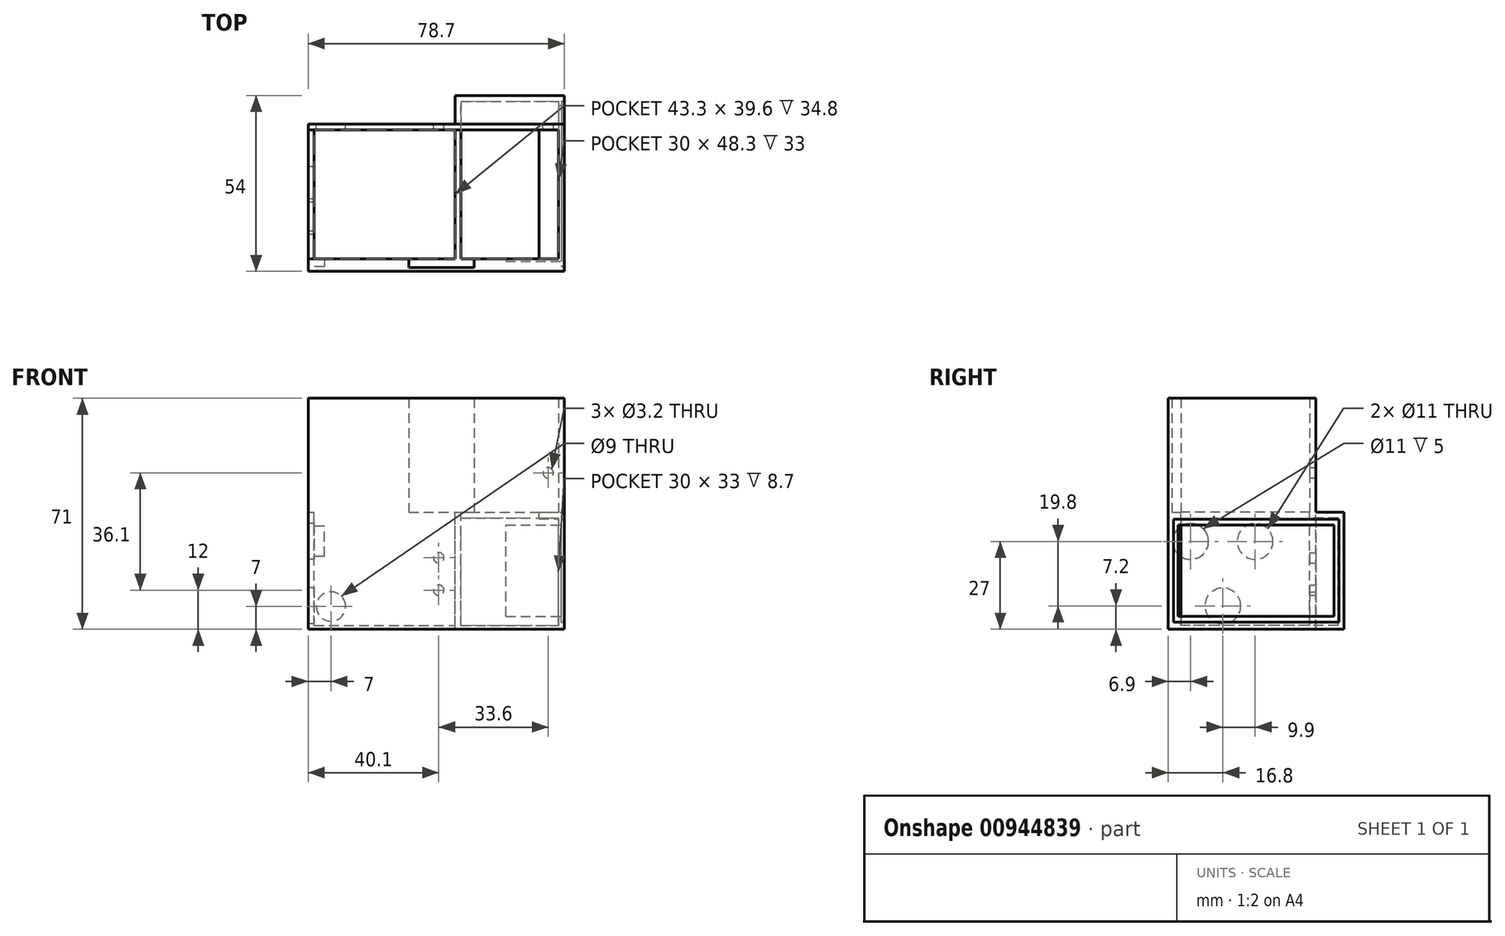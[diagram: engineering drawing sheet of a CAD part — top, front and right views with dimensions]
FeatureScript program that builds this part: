
annotation { "Feature Type Name" : "Feature", "Feature Type Description" : "" }
export const myFeature = defineFeature(function(context is Context, id is Id, definition is map)
    precondition{}
    {
        {
            var Q0;
            Q0=qCreatedBy(makeId("Top.planeOp"),FACE);
            var sketch = newSketch(context, id + "F0", { "sketchPlane" : qUnion([Q0])});
            skLineSegment(sketch, "E0.bottom", {"start": v(-38.45, 19.8) * mm, "end": v(38.45, 19.8) * mm});
            skLineSegment(sketch, "E0.top", {"start": v(-38.45, -19.8) * mm, "end": v(38.45, -19.8) * mm});
            skLineSegment(sketch, "E0.left", {"start": v(-38.45, 19.8) * mm, "end": v(-38.45, -19.8) * mm});
            skLineSegment(sketch, "E0.right", {"start": v(38.45, 19.8) * mm, "end": v(38.45, -19.8) * mm});
            skPoint(sketch, "E0.middle", {"position": v(0, 0) * mm});
            skLineSegment(sketch, "E1", {"start": v(-38.45, 19.8) * mm, "end": v(-38.45, 21.6) * mm});
            skLineSegment(sketch, "E2", {"start": v(-38.45, 21.6) * mm, "end": v(40.25, 21.6) * mm});
            skLineSegment(sketch, "E3", {"start": v(40.25, 21.6) * mm, "end": v(40.25, -23.7) * mm});
            skLineSegment(sketch, "E4", {"start": v(40.25, -23.7) * mm, "end": v(-38.45, -23.7) * mm});
            skLineSegment(sketch, "E5", {"start": v(-38.45, -23.7) * mm, "end": v(-38.45, -19.8) * mm});
            skLineSegment(sketch, "E6", {"start": v(-7.55, -19.8) * mm, "end": v(-7.55, -22.5) * mm});
            skLineSegment(sketch, "E7", {"start": v(-7.55, -22.5) * mm, "end": v(12.45, -22.5) * mm});
            skLineSegment(sketch, "E8", {"start": v(12.45, -22.5) * mm, "end": v(12.45, -19.8) * mm});
            skLineSegment(sketch, "E9", {"start": v(-36.65, 19.8) * mm, "end": v(-36.65, -19.8) * mm});
            skLineSegment(sketch, "E10", {"start": v(8.45, 19.8) * mm, "end": v(8.45, -19.8) * mm});
            skLineSegment(sketch, "E11", {"start": v(6.65, 19.8) * mm, "end": v(6.65, -19.8) * mm});
            skLineSegment(sketch, "E12", {"start": v(40.25, 21.6) * mm, "end": v(40.25, 30.3) * mm});
            skLineSegment(sketch, "E13", {"start": v(40.25, 30.3) * mm, "end": v(6.65, 30.3) * mm});
            skLineSegment(sketch, "E14", {"start": v(6.65, 30.3) * mm, "end": v(6.65, 21.6) * mm});
            skLineSegment(sketch, "E15", {"start": v(8.45, 21.6) * mm, "end": v(8.45, 28.5) * mm});
            skLineSegment(sketch, "E16", {"start": v(8.45, 28.5) * mm, "end": v(38.45, 28.5) * mm});
            skLineSegment(sketch, "E17", {"start": v(38.45, 28.5) * mm, "end": v(38.45, 21.6) * mm});
            skLineSegment(sketch, "E18", {"start": v(38.45, 21.6) * mm, "end": v(38.45, 19.8) * mm});
            skLineSegment(sketch, "E19", {"start": v(8.45, 21.6) * mm, "end": v(8.45, 19.8) * mm});
            skLineSegment(sketch, "E20", {"start": v(32.45, -19.8) * mm, "end": v(32.45, 19.8) * mm});
            skSolve(sketch);
        }
        {
            var Q0;
            {var subQ0=sQuery(id+"F0.wireOp",EDGE,"E1");Q0=makeQuery(id+"F0.imprint","IMPRINT",FACE,{"disambiguationData":[TD([[makeQuery(id+"F0.imprint","IMPRINT",EDGE,{"derivedFrom":subQ0}),-1.0]])]});}
            var Q1;
            {var subQ0=sQuery(id+"F0.wireOp",EDGE,"E18");Q1=makeQuery(id+"F0.imprint","IMPRINT",FACE,{"disambiguationData":[TD([[makeQuery(id+"F0.imprint","IMPRINT",EDGE,{"derivedFrom":subQ0}),-1.0]])]});}
            var Q2;
            {var subQ5=sQuery(id+"F0.wireOp",EDGE,"E0.right");Q2=makeQuery(id+"F0.imprint","IMPRINT",FACE,{"disambiguationData":[TD([[makeQuery(id+"F0.imprint","IMPRINT",EDGE,{"derivedFrom":subQ5}),1.0]])]});}
            extrude(context, id + "F1", {"entities" : qUnion([Q0, Q1, Q2]), "depth" : 35 * mm, "offsetDistance" : 25 * mm});
        }
        {
            var Q0;
            {var subQ0=sQuery(id+"F0.wireOp",EDGE,"E0.left");Q0=makeQuery(id+"F0.imprint","IMPRINT",FACE,{"disambiguationData":[TD([[makeQuery(id+"F0.imprint","IMPRINT",EDGE,{"derivedFrom":subQ0}),1.0]])]});}
            var Q1;
            {var subQ0=sQuery(id+"F0.wireOp",EDGE,"E1");Q1=makeQuery(id+"F0.imprint","IMPRINT",FACE,{"disambiguationData":[TD([[makeQuery(id+"F0.imprint","IMPRINT",EDGE,{"derivedFrom":subQ0}),-1.0]])]});}
            var Q2;
            {var subQ0=sQuery(id+"F0.wireOp",EDGE,"E12");Q2=makeQuery(id+"F0.imprint","IMPRINT",FACE,{"disambiguationData":[TD([[makeQuery(id+"F0.imprint","IMPRINT",EDGE,{"derivedFrom":subQ0}),1.0]])]});}
            var Q3;
            {var subQ5=sQuery(id+"F0.wireOp",EDGE,"E0.right");Q3=makeQuery(id+"F0.imprint","IMPRINT",FACE,{"disambiguationData":[TD([[makeQuery(id+"F0.imprint","IMPRINT",EDGE,{"derivedFrom":subQ5}),1.0]])]});}
            var Q4;
            {var subQ0=sQuery(id+"F0.wireOp",EDGE,"E6");Q4=makeQuery(id+"F0.imprint","IMPRINT",FACE,{"disambiguationData":[TD([[makeQuery(id+"F0.imprint","IMPRINT",EDGE,{"derivedFrom":subQ0}),1.0]])]});}
            var Q5;
            {var subQ0=sQuery(id+"F0.wireOp",EDGE,"E10");Q5=makeQuery(id+"F0.imprint","IMPRINT",FACE,{"disambiguationData":[TD([[makeQuery(id+"F0.imprint","IMPRINT",EDGE,{"derivedFrom":subQ0}),-1.0]])]});}
            extrude(context, id + "F2", {"entities" : qUnion([Q0, Q1, Q2, Q3, Q4, Q5]), "operationType" : NewBodyOperationType.ADD, "oppositeDirection" : true, "depth" : 36 * mm, "offsetDistance" : 25 * mm});
        }
        {
            var Q0;
            {var subQ0=sQuery(id+"F0.wireOp",EDGE,"E15");Q0=makeQuery(id+"F0.imprint","IMPRINT",FACE,{"disambiguationData":[TD([[makeQuery(id+"F0.imprint","IMPRINT",EDGE,{"derivedFrom":subQ0}),-1.0]])]});}
            var Q1;
            {var subQ0=sQuery(id+"F0.wireOp",EDGE,"E18");Q1=makeQuery(id+"F0.imprint","IMPRINT",FACE,{"disambiguationData":[TD([[makeQuery(id+"F0.imprint","IMPRINT",EDGE,{"derivedFrom":subQ0}),-1.0]])]});}
            extrude(context, id + "F3", {"entities" : qUnion([Q0, Q1]), "operationType" : NewBodyOperationType.ADD, "oppositeDirection" : true, "depth" : 1.8 * mm, "offsetDistance" : 25 * mm});
        }
        {
            var Q0;
            {var subQ0=sQuery(id+"F0.wireOp",EDGE,"E3");Q0=makeQuery(id+"F2.boolean.opBoolean","MERGE",FACE,{"derivedFrom":[makeQuery(id+"F1.opExtrude","SWEPT_FACE",FACE,{"disambiguationData":[OSD([subQ0])]}),makeQuery(id+"F2.opExtrude","SWEPT_FACE",FACE,{"disambiguationData":[OSD([subQ0,sQuery(id+"F0.wireOp",EDGE,"E12")])]})]});}
            var sketch = newSketch(context, id + "F4", { "sketchPlane" : qUnion([Q0])});
            skLineSegment(sketch, "E21.bottom", {"start": v(28.7, -33.8) * mm, "end": v(-22.1, -33.8) * mm});
            skLineSegment(sketch, "E21.top", {"start": v(28.7, -2.2) * mm, "end": v(-22.1, -2.2) * mm});
            skLineSegment(sketch, "E21.left", {"start": v(28.7, -33.8) * mm, "end": v(28.7, -2.2) * mm});
            skLineSegment(sketch, "E21.right", {"start": v(-22.1, -33.8) * mm, "end": v(-22.1, -2.2) * mm});
            skPoint(sketch, "E21.middle", {"position": v(3.3, -18) * mm});
            skPoint(sketch, "E21.middle.positionSnap0", {"position": v(30.3, -18) * mm});
            skPoint(sketch, "E21.middle.positionSnap1", {"position": v(3.3, -36) * mm});
            skPoint(sketch, "E21.centerSnap0", {"position": v(30.3, -18) * mm});
            skPoint(sketch, "E21.centerSnap1", {"position": v(3.3, -36) * mm});
            skLineSegment(sketch, "E22.bottom", {"start": v(27.2, -32) * mm, "end": v(-20.6, -32) * mm});
            skLineSegment(sketch, "E22.top", {"start": v(27.2, -4) * mm, "end": v(-20.6, -4) * mm});
            skLineSegment(sketch, "E22.left", {"start": v(27.2, -32) * mm, "end": v(27.2, -4) * mm});
            skLineSegment(sketch, "E22.right", {"start": v(-20.6, -32) * mm, "end": v(-20.6, -4) * mm});
            skSolve(sketch);
        }
        {
            var Q0;
            Q0=makeQuery(id+"F4.imprint","IMPRINT",FACE,{"disambiguationData":[TD([[makeQuery(id+"F4.imprint","IMPRINT",EDGE,{"derivedFrom":sQuery(id+"F4.wireOp",EDGE,"E22.bottom")}),-1.0]])]});
            extrude(context, id + "F5", {"entities" : qUnion([Q0]), "operationType" : NewBodyOperationType.REMOVE, "oppositeDirection" : true, "depth" : 18 * mm, "offsetDistance" : 25 * mm});
        }
        {
            var Q0;
            Q0=makeQuery(id+"F4.imprint","IMPRINT",FACE,{"disambiguationData":[TD([[makeQuery(id+"F4.imprint","IMPRINT",EDGE,{"derivedFrom":sQuery(id+"F4.wireOp",EDGE,"E21.bottom")}),-1.0]])]});
            extrude(context, id + "F6", {"entities" : qUnion([Q0]), "operationType" : NewBodyOperationType.REMOVE, "oppositeDirection" : true, "depth" : 1 * mm, "offsetDistance" : 25 * mm});
        }
        {
            var Q0;
            Q0=makeQuery(id+"F2.opExtrude","CAP_FACE",FACE,{"disambiguationData":[OSD([sQuery(id+"F0.wireOp",EDGE,"E0.bottom"),sQuery(id+"F0.wireOp",EDGE,"E0.top"),sQuery(id+"F0.wireOp",EDGE,"E0.left"),sQuery(id+"F0.wireOp",EDGE,"E0.right"),sQuery(id+"F0.wireOp",EDGE,"E1"),sQuery(id+"F0.wireOp",EDGE,"E2"),sQuery(id+"F0.wireOp",EDGE,"E3"),sQuery(id+"F0.wireOp",EDGE,"E4"),sQuery(id+"F0.wireOp",EDGE,"E5"),sQuery(id+"F0.wireOp",EDGE,"E9"),sQuery(id+"F0.wireOp",EDGE,"E10"),sQuery(id+"F0.wireOp",EDGE,"E11"),sQuery(id+"F0.wireOp",EDGE,"E12"),sQuery(id+"F0.wireOp",EDGE,"E13"),sQuery(id+"F0.wireOp",EDGE,"E14"),sQuery(id+"F0.wireOp",EDGE,"E15"),sQuery(id+"F0.wireOp",EDGE,"E16"),sQuery(id+"F0.wireOp",EDGE,"E17"),sQuery(id+"F0.wireOp",EDGE,"E18"),sQuery(id+"F0.wireOp",EDGE,"E19")])],"isStart":false});
            var sketch = newSketch(context, id + "F7", { "sketchPlane" : qUnion([Q0])});
            skSolve(sketch);
        }
        {
            var Q0;
            Q0=makeQuery(id+"F7.imprint","IMPRINT",FACE,{"disambiguationData":[TD([[makeQuery(id+"F7.imprint","IMPRINT",EDGE,{"derivedFrom":makeQuery(id+"F2.opExtrude","CAP_EDGE",EDGE,{"disambiguationData":[OSD([sQuery(id+"F0.wireOp",EDGE,"E0.bottom")])],"isStart":false})}),1.0]])]});
            var Q1;
            Q1=makeQuery(id+"F7.imprint","IMPRINT",FACE,{"disambiguationData":[TD([[makeQuery(id+"F7.imprint","IMPRINT",EDGE,{"derivedFrom":makeQuery(id+"F2.opExtrude","CAP_EDGE",EDGE,{"disambiguationData":[OSD([sQuery(id+"F0.wireOp",EDGE,"E16")])],"isStart":false})}),1.0]])]});
            extrude(context, id + "F8", {"entities" : qUnion([Q0, Q1]), "operationType" : NewBodyOperationType.ADD, "oppositeDirection" : true, "depth" : 1.2 * mm, "offsetDistance" : 25 * mm});
        }
        {
            var Q0;
            {var subQ0=sQuery(id+"F0.wireOp",EDGE,"E0.right");Q0=makeQuery(id+"F0.imprint","IMPRINT",FACE,{"disambiguationData":[TD([[makeQuery(id+"F0.imprint","IMPRINT",EDGE,{"derivedFrom":subQ0}),-1.0]])]});}
            extrude(context, id + "F9", {"entities" : qUnion([Q0]), "operationType" : NewBodyOperationType.ADD, "oppositeDirection" : true, "depth" : 2 * mm, "offsetDistance" : 25 * mm});
        }
        {
            var Q0;
            {var subQ0=sQuery(id+"F0.wireOp",EDGE,"E2");Q0=makeQuery(id+"F2.boolean.opBoolean","MERGE",FACE,{"derivedFrom":[makeQuery(id+"F1.opExtrude","SWEPT_FACE",FACE,{"disambiguationData":[OSD([subQ0])]}),makeQuery(id+"F2.opExtrude","SWEPT_FACE",FACE,{"disambiguationData":[OSD([subQ0])]})]});}
            var sketch = newSketch(context, id + "F10", { "sketchPlane" : qUnion([Q0])});
            skCircle(sketch, "E23", {"center": v(-35.25, 12.1) * mm, "radius": 1.6 * mm});
            skCircle(sketch, "E24", {"center": v(-1.65, -14) * mm, "radius": 1.6 * mm});
            skCircle(sketch, "E25", {"center": v(-1.65, -24) * mm, "radius": 1.6 * mm});
            skCircle(sketch, "E26", {"center": v(31.45, -29) * mm, "radius": 4.5 * mm});
            skSolve(sketch);
        }
        {
            var Q0;
            Q0=makeQuery(id+"F10.imprint","IMPRINT",FACE,{"disambiguationData":[TD([[makeQuery(id+"F10.imprint","IMPRINT",EDGE,{"derivedFrom":sQuery(id+"F10.wireOp",EDGE,"E23")}),1.0]])]});
            extrude(context, id + "F11", {"entities" : qUnion([Q0]), "operationType" : NewBodyOperationType.REMOVE, "oppositeDirection" : true, "depth" : 2 * mm, "offsetDistance" : 25 * mm});
        }
        {
            var Q0;
            {var subQ0=sQuery(id+"F0.wireOp",EDGE,"E5");var subQ1=sQuery(id+"F0.wireOp",EDGE,"E1");Q0=makeQuery(id+"F2.boolean.opBoolean","MERGE",FACE,{"derivedFrom":[makeQuery(id+"F1.opExtrude","SWEPT_FACE",FACE,{"disambiguationData":[OSD([subQ1])]}),makeQuery(id+"F1.opExtrude","SWEPT_FACE",FACE,{"disambiguationData":[OSD([subQ0])]}),makeQuery(id+"F2.opExtrude","SWEPT_FACE",FACE,{"disambiguationData":[OSD([sQuery(id+"F0.wireOp",EDGE,"E0.left"),subQ1,subQ0])]})]});}
            var sketch = newSketch(context, id + "F12", { "sketchPlane" : qUnion([Q0])});
            skCircle(sketch, "E27", {"center": v(-3, -9) * mm, "radius": 5.5 * mm});
            skCircle(sketch, "E28", {"center": v(16.8, -9) * mm, "radius": 5.5 * mm});
            skCircle(sketch, "E29", {"center": v(6.9, -28.8) * mm, "radius": 5.5 * mm});
            skSolve(sketch);
        }
        {
            var Q0;
            Q0=makeQuery(id+"F12.imprint","IMPRINT",FACE,{"disambiguationData":[TD([[makeQuery(id+"F12.imprint","IMPRINT",EDGE,{"derivedFrom":sQuery(id+"F12.wireOp",EDGE,"E27")}),1.0]])]});
            var Q1;
            Q1=makeQuery(id+"F12.imprint","IMPRINT",FACE,{"disambiguationData":[TD([[makeQuery(id+"F12.imprint","IMPRINT",EDGE,{"derivedFrom":sQuery(id+"F12.wireOp",EDGE,"E28")}),1.0]])]});
            var Q2;
            Q2=makeQuery(id+"F12.imprint","IMPRINT",FACE,{"disambiguationData":[TD([[makeQuery(id+"F12.imprint","IMPRINT",EDGE,{"derivedFrom":sQuery(id+"F12.wireOp",EDGE,"E29")}),1.0]])]});
            extrude(context, id + "F13", {"entities" : qUnion([Q0, Q1, Q2]), "operationType" : NewBodyOperationType.REMOVE, "oppositeDirection" : true, "depth" : 5 * mm, "offsetDistance" : 25 * mm});
        }
        {
            var Q0;
            Q0=makeQuery(id+"F10.imprint","IMPRINT",FACE,{"disambiguationData":[TD([[makeQuery(id+"F10.imprint","IMPRINT",EDGE,{"derivedFrom":sQuery(id+"F10.wireOp",EDGE,"E24")}),1.0]])]});
            var Q1;
            Q1=makeQuery(id+"F10.imprint","IMPRINT",FACE,{"disambiguationData":[TD([[makeQuery(id+"F10.imprint","IMPRINT",EDGE,{"derivedFrom":sQuery(id+"F10.wireOp",EDGE,"E25")}),1.0]])]});
            var Q2;
            Q2=makeQuery(id+"F10.imprint","IMPRINT",FACE,{"disambiguationData":[TD([[makeQuery(id+"F10.imprint","IMPRINT",EDGE,{"derivedFrom":sQuery(id+"F10.wireOp",EDGE,"E26")}),1.0]])]});
            extrude(context, id + "F14", {"entities" : qUnion([Q0, Q1, Q2]), "operationType" : NewBodyOperationType.REMOVE, "oppositeDirection" : true, "depth" : 2 * mm, "offsetDistance" : 25 * mm});
        }
    });
